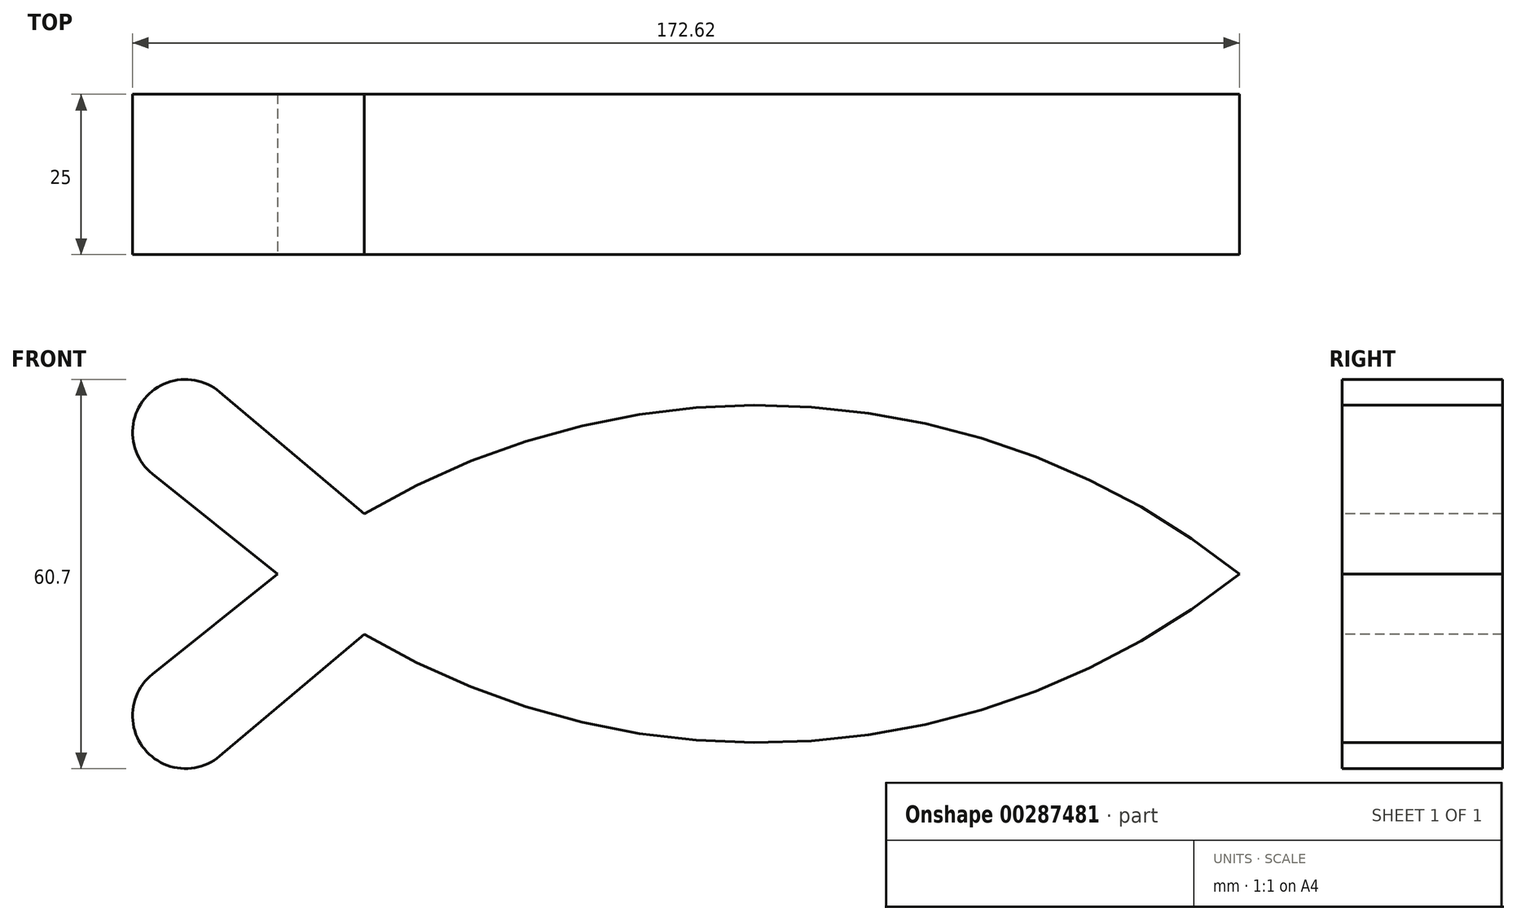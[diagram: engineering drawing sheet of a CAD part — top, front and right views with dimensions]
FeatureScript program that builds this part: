
annotation { "Feature Type Name" : "Feature", "Feature Type Description" : "" }
export const myFeature = defineFeature(function(context is Context, id is Id, definition is map)
    precondition{}
    {
        {
            var Q0;
            Q0=qCreatedBy(makeId("Front.planeOp"),FACE);
            var sketch = newSketch(context, id + "F0", { "sketchPlane" : qUnion([Q0])});
            skArc(sketch, "E0", {"start": v(150, 0) * mm, "mid": v(75, 26.33) * mm, "end": v(0, 0) * mm});
            skArc(sketch, "E1.MirrorCS", {"start": v(150, 0) * mm, "mid": v(75, -26.33) * mm, "end": v(0, 0) * mm});
            skLineSegment(sketch, "E2", {"start": v(0, 0) * mm, "end": v(-19.52, 15.62) * mm});
            skArc(sketch, "E3", {"start": v(-19.52, 15.62) * mm, "mid": v(-20.73, 27.34) * mm, "end": v(-9, 28.4) * mm});
            skLineSegment(sketch, "E4", {"start": v(-9, 28.4) * mm, "end": v(13.52, 9.38) * mm});
            skLineSegment(sketch, "E5.MirrorCS", {"start": v(-9, -28.4) * mm, "end": v(13.52, -9.38) * mm});
            skArc(sketch, "E6.MirrorCS", {"start": v(-19.52, -15.62) * mm, "mid": v(-20.73, -27.34) * mm, "end": v(-9, -28.4) * mm});
            skLineSegment(sketch, "E7.MirrorCS", {"start": v(0, 0) * mm, "end": v(-19.52, -15.62) * mm});
            skSolve(sketch);
        }
        {
            var Q0;
            {var subQ0=sQuery(id+"F0.wireOp",EDGE,"E1.MirrorCS");var subQ1=sQuery(id+"F0.wireOp",EDGE,"E0");var subQ2=makeQuery(id+"F0.imprint","INTERSECT",VERTEX,{"derivedFrom":[subQ1,subQ0]});Q0=makeQuery(id+"F0.imprint","IMPRINT",FACE,{"disambiguationData":[TD([[makeQuery(id+"F0.imprint","IMPRINT",EDGE,{"disambiguationData":[TD([[subQ2,-1.0]])],"derivedFrom":subQ1}),1.0]])]});}
            var Q1;
            {var subQ0=sQuery(id+"F0.wireOp",EDGE,"E2");Q1=makeQuery(id+"F0.imprint","IMPRINT",FACE,{"disambiguationData":[TD([[makeQuery(id+"F0.imprint","IMPRINT",EDGE,{"derivedFrom":subQ0}),-1.0]])]});}
            var Q2;
            {var subQ2=sQuery(id+"F0.wireOp",EDGE,"E5.MirrorCS");Q2=makeQuery(id+"F0.imprint","IMPRINT",FACE,{"disambiguationData":[TD([[makeQuery(id+"F0.imprint","IMPRINT",EDGE,{"derivedFrom":subQ2}),1.0]])]});}
            extrude(context, id + "F1", {"entities" : qUnion([Q0, Q1, Q2]), "oppositeDirection" : true, "depth" : 25 * mm});
        }
    });
